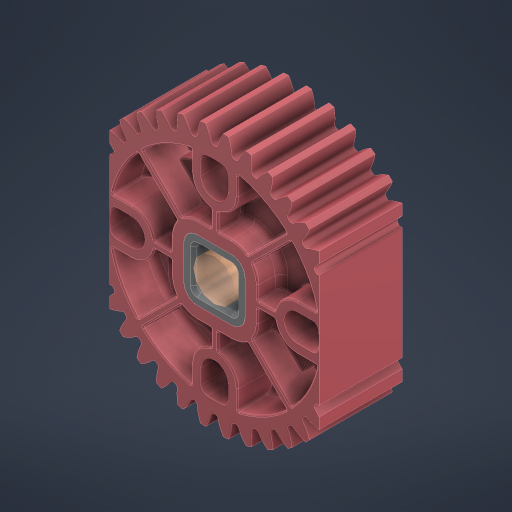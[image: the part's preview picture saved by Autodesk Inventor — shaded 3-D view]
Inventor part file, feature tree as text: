
AUTODESK INVENTOR PART (.ipt)
format: ipt  version: 2024 (Build 280153000, 153)  size: 2,299,904 bytes
history: native  units: in
note: dims shown in document units (in); Inventor stores cm internally (conversion verified against a paired STEP export)
features: other x3, extrude x2, sketch x1
ambient origin geometry x8: Origin, YZ Plane, XZ Plane, XY Plane, X Axis, Y Axis, Z Axis, Center Point
bodies: Solid1 (feature_tree), Solid2 (feature_tree)
feature tree (6):
  extrude  "Extrusion1"  Depth=0.3937in TaperAngle=0.0deg
  other  "Srf1"
  sketch  "Sketch4"  dims[d0=0.25in d1=0.3937in d2=0.0in d3=0.63in d4=0.0in d5=0.0in]
  other  "276-7747-001_OVERMOLD Rev3_36T 24DP Gear Rev1_1:1"
  other  "276-7573-002 Rev7_2:1"
  extrude  "ExtrusionSrf1"  Depth=0.3937in
